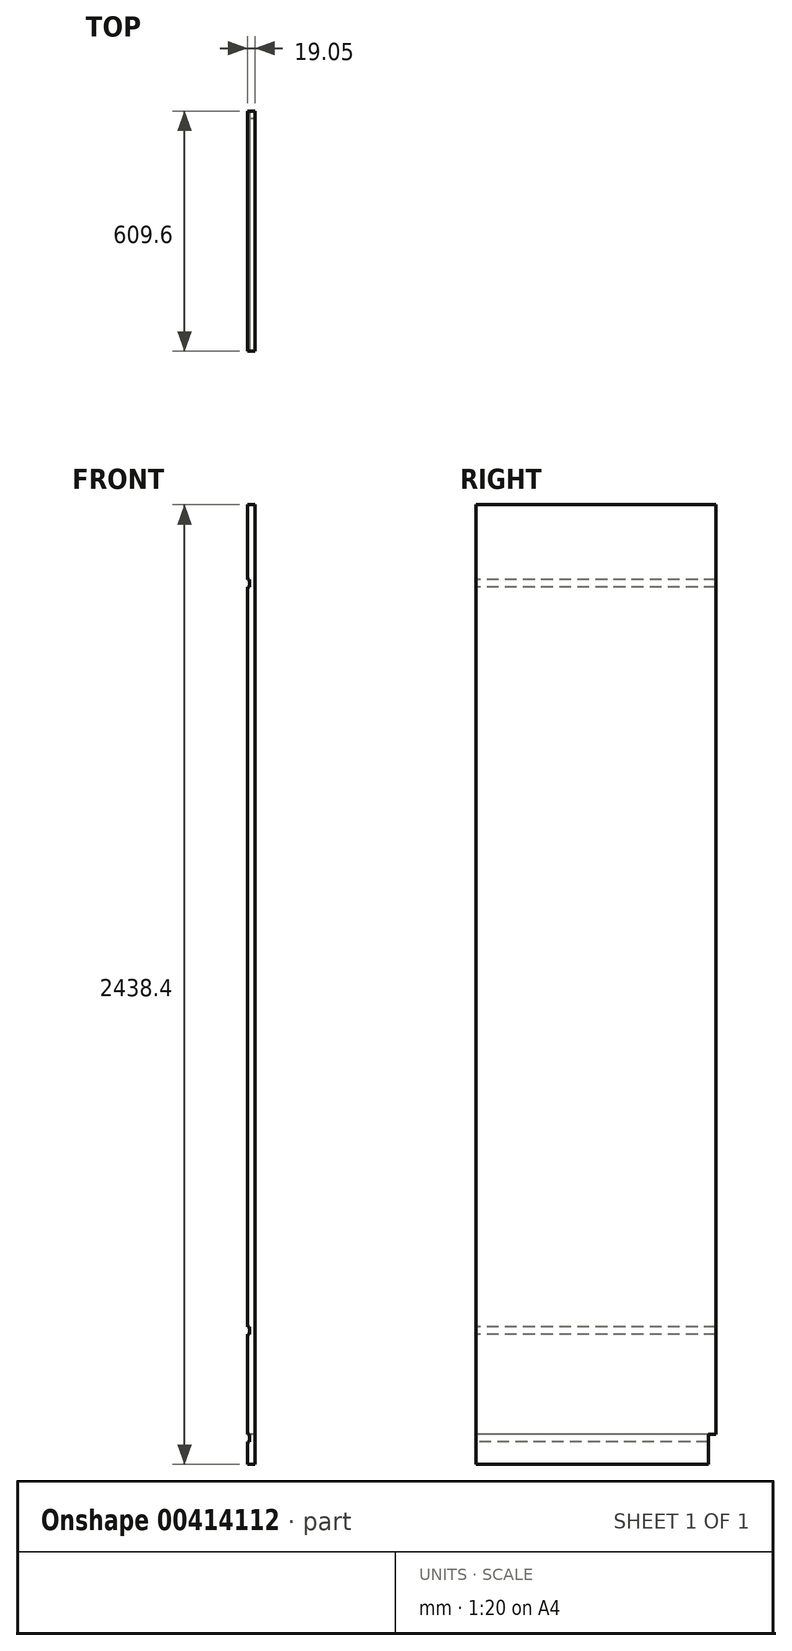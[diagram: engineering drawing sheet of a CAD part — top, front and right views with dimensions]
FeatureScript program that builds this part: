
annotation { "Feature Type Name" : "Feature", "Feature Type Description" : "" }
export const myFeature = defineFeature(function(context is Context, id is Id, definition is map)
    precondition{}
    {
        {
            var Q0;
            Q0=qCreatedBy(makeId("Right.planeOp"),FACE);
            var sketch = newSketch(context, id + "F0", { "sketchPlane" : qUnion([Q0])});
            skLineSegment(sketch, "E0.bottom", {"start": v(304.8, -1219.2) * mm, "end": v(-304.8, -1219.2) * mm});
            skLineSegment(sketch, "E0.top", {"start": v(304.8, 1219.2) * mm, "end": v(-304.8, 1219.2) * mm});
            skLineSegment(sketch, "E0.left", {"start": v(304.8, -1219.2) * mm, "end": v(304.8, 1219.2) * mm});
            skLineSegment(sketch, "E0.right", {"start": v(-304.8, -1219.2) * mm, "end": v(-304.8, 1219.2) * mm});
            skPoint(sketch, "E0.middle", {"position": v(0, 0) * mm});
            skSolve(sketch);
        }
        {
            var Q0;
            Q0=makeQuery(id+"F0.imprint","IMPRINT",FACE,{"disambiguationData":[TD([[makeQuery(id+"F0.imprint","IMPRINT",EDGE,{"derivedFrom":sQuery(id+"F0.wireOp",EDGE,"E0.bottom")}),-1.0]])]});
            extrude(context, id + "F1", {"entities" : qUnion([Q0]), "depth" : 19.05 * mm});
        }
        {
            var Q0;
            Q0=makeQuery(id+"F1.opExtrude","CAP_FACE",FACE,{"disambiguationData":[OSD([sQuery(id+"F0.wireOp",EDGE,"E0.bottom"),sQuery(id+"F0.wireOp",EDGE,"E0.top"),sQuery(id+"F0.wireOp",EDGE,"E0.left"),sQuery(id+"F0.wireOp",EDGE,"E0.right")])],"isStart":true});
            var sketch = newSketch(context, id + "F2", { "sketchPlane" : qUnion([Q0])});
            skLineSegment(sketch, "E1.bottom", {"start": v(-304.8, -1219.2) * mm, "end": v(-285.75, -1219.2) * mm});
            skLineSegment(sketch, "E1.top", {"start": v(-304.8, -1143) * mm, "end": v(-285.75, -1143) * mm});
            skLineSegment(sketch, "E1.left", {"start": v(-304.8, -1219.2) * mm, "end": v(-304.8, -1143) * mm});
            skLineSegment(sketch, "E1.right", {"start": v(-285.75, -1219.2) * mm, "end": v(-285.75, -1143) * mm});
            skSolve(sketch);
        }
        {
            var Q0;
            Q0 = qSketchRegion(id + "F2", true);
            extrude(context, id + "F3", {"entities" : qUnion([Q0]), "operationType" : NewBodyOperationType.REMOVE, "oppositeDirection" : true, "depth" : 25.4 * mm});
        }
        {
            var Q0;
            Q0=makeQuery(id+"F1.opExtrude","SWEPT_FACE",FACE,{"disambiguationData":[OSD([sQuery(id+"F0.wireOp",EDGE,"E0.right")])]});
            var sketch = newSketch(context, id + "F4", { "sketchPlane" : qUnion([Q0])});
            skLineSegment(sketch, "E2.bottom", {"start": v(0, -1143) * mm, "end": v(4.76, -1143) * mm});
            skLineSegment(sketch, "E2.top", {"start": v(0, -1162.05) * mm, "end": v(4.76, -1162.05) * mm});
            skLineSegment(sketch, "E2.left", {"start": v(0, -1143) * mm, "end": v(0, -1162.05) * mm});
            skLineSegment(sketch, "E2.right", {"start": v(4.76, -1143) * mm, "end": v(4.76, -1162.05) * mm});
            skLineSegment(sketch, "E3.bottom", {"start": v(0, -869.95) * mm, "end": v(4.76, -869.95) * mm});
            skLineSegment(sketch, "E3.top", {"start": v(0, -889) * mm, "end": v(4.76, -889) * mm});
            skLineSegment(sketch, "E3.left", {"start": v(0, -869.95) * mm, "end": v(0, -889) * mm});
            skLineSegment(sketch, "E3.right", {"start": v(4.76, -869.95) * mm, "end": v(4.76, -889) * mm});
            skLineSegment(sketch, "E4.bottom", {"start": v(0, 1028.7) * mm, "end": v(4.76, 1028.7) * mm});
            skLineSegment(sketch, "E4.top", {"start": v(0, 1009.65) * mm, "end": v(4.76, 1009.65) * mm});
            skLineSegment(sketch, "E4.left", {"start": v(0, 1028.7) * mm, "end": v(0, 1009.65) * mm});
            skLineSegment(sketch, "E4.right", {"start": v(4.76, 1028.7) * mm, "end": v(4.76, 1009.65) * mm});
            skSolve(sketch);
        }
        {
            var Q0;
            Q0 = qSketchRegion(id + "F4", true);
            extrude(context, id + "F5", {"entities" : qUnion([Q0]), "operationType" : NewBodyOperationType.REMOVE, "endBound" : BoundingType.THROUGH_ALL, "oppositeDirection" : true, "depth" : 25.4 * mm});
        }
    });
